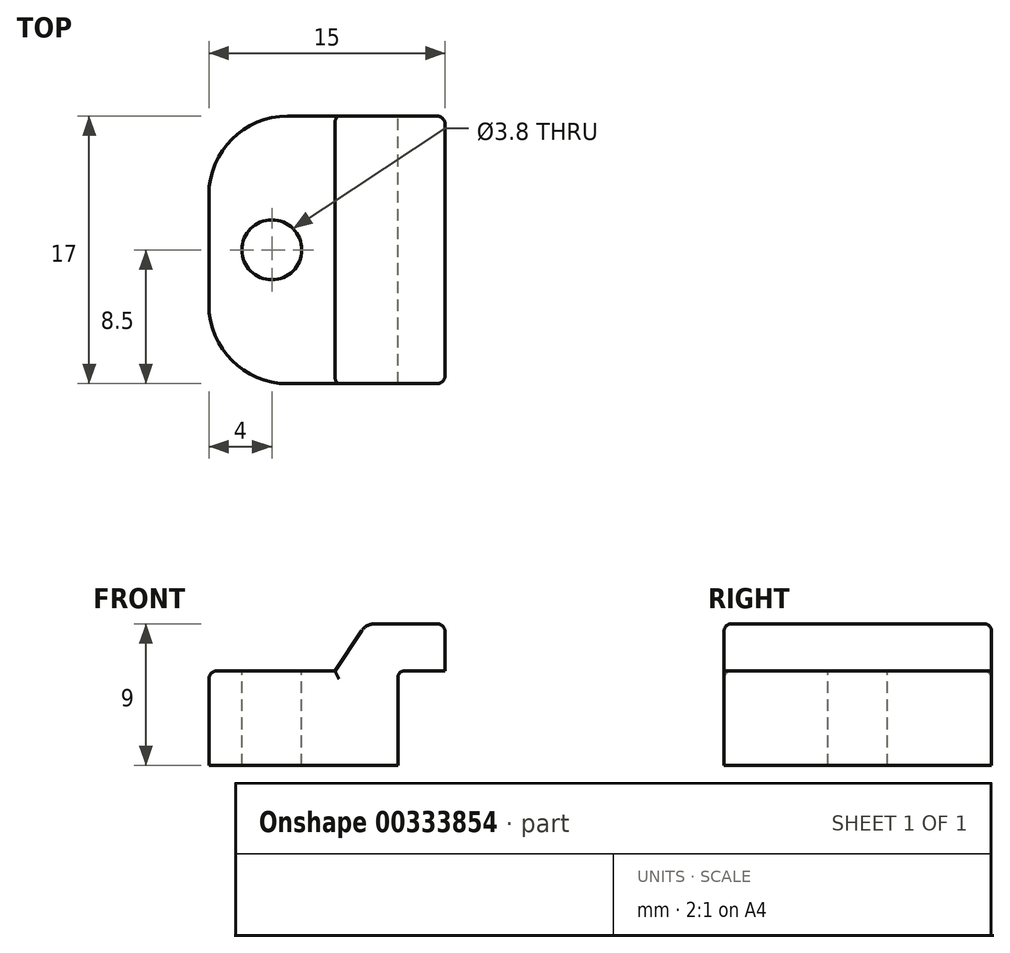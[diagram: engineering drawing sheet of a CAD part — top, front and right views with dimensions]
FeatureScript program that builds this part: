
annotation { "Feature Type Name" : "Feature", "Feature Type Description" : "" }
export const myFeature = defineFeature(function(context is Context, id is Id, definition is map)
    precondition{}
    {
        {
            var Q0;
            Q0=qCreatedBy(makeId("Front.planeOp"),FACE);
            var sketch = newSketch(context, id + "F0", { "sketchPlane" : qUnion([Q0])});
            skLineSegment(sketch, "E0", {"start": v(0, 0) * mm, "end": v(0, 5.59) * mm});
            skLineSegment(sketch, "E1", {"start": v(0.41, 6) * mm, "end": v(3, 6) * mm});
            skLineSegment(sketch, "E2", {"start": v(3, 6) * mm, "end": v(3, 9) * mm});
            skLineSegment(sketch, "E3", {"start": v(0, 0) * mm, "end": v(-12, 0) * mm});
            skLineSegment(sketch, "E4", {"start": v(-12, 0) * mm, "end": v(-12, 6) * mm});
            skLineSegment(sketch, "E5", {"start": v(-12, 6) * mm, "end": v(-2.83, 6) * mm});
            skLineSegment(sketch, "E6", {"start": v(3, 9) * mm, "end": v(-2, 9) * mm});
            skPoint(sketch, "E7.visualSharp", {"position": v(-4, 6) * mm});
            skPoint(sketch, "E8.visualSharp", {"position": v(1, 9) * mm});
            skPoint(sketch, "E9.visualSharp", {"position": v(0, 6) * mm});
            skArc(sketch, "E9.filletArc", {"start": v(0.41, 6) * mm, "mid": v(0.12, 5.88) * mm, "end": v(0, 5.59) * mm});
            skLineSegment(sketch, "E10", {"start": v(-4, 6) * mm, "end": v(-2.83, 6) * mm});
            skLineSegment(sketch, "E11", {"start": v(-2, 9) * mm, "end": v(-4, 6) * mm});
            skSolve(sketch);
        }
        {
            var Q0;
            Q0 = qSketchRegion(id + "F0", true);
            extrude(context, id + "F1", {"entities" : qUnion([Q0]), "depth" : 17 * mm});
        }
        {
            var Q0;
            Q0=makeQuery(id+"F1.opExtrude","SWEPT_EDGE",EDGE,{"disambiguationData":[OSD([sQuery(id+"F0.wireOp",EDGE,"E2"),sQuery(id+"F0.wireOp",EDGE,"E6")])]});
            fillet(context, id + "F2", {"entities" : qUnion([Q0]), "radius" : 0.5 * mm, "tangentPropagation" : true, "allowEdgeOverflow" : false});
        }
        {
            var Q0;
            Q0=makeQuery(id+"F1.opExtrude","SWEPT_FACE",FACE,{"disambiguationData":[OSD([sQuery(id+"F0.wireOp",EDGE,"E5")])]});
            var sketch = newSketch(context, id + "F3", { "sketchPlane" : qUnion([Q0])});
            skCircle(sketch, "E12", {"center": v(-8, -8.5) * mm, "radius": 1.9 * mm});
            skPoint(sketch, "E12.centerSnap0", {"position": v(-8, -17) * mm});
            skPoint(sketch, "E12.centerSnap1", {"position": v(-12, -8.5) * mm});
            skSolve(sketch);
        }
        {
            var Q0;
            Q0 = qSketchRegion(id + "F3", true);
            extrude(context, id + "F4", {"entities" : qUnion([Q0]), "operationType" : NewBodyOperationType.REMOVE, "oppositeDirection" : true, "depth" : 25 * mm});
        }
        {
            var Q0;
            Q0=makeQuery(id+"F1.opExtrude","CAP_EDGE",EDGE,{"disambiguationData":[OSD([sQuery(id+"F0.wireOp",EDGE,"E4")])],"isStart":false});
            var Q1;
            Q1=makeQuery(id+"F1.opExtrude","CAP_EDGE",EDGE,{"disambiguationData":[OSD([sQuery(id+"F0.wireOp",EDGE,"E4")])],"isStart":true});
            fillet(context, id + "F5", {"entities" : qUnion([Q0, Q1]), "radius" : 5 * mm, "tangentPropagation" : true, "allowEdgeOverflow" : false});
        }
        {
            var Q0;
            Q0=makeQuery(id+"F5.opFillet","BLEND_EDGE",EDGE,{"blendedFrom":[makeQuery(id+"F1.opExtrude","CAP_EDGE",EDGE,{"disambiguationData":[OSD([sQuery(id+"F0.wireOp",EDGE,"E4")])],"isStart":false}),makeQuery(id+"F1.opExtrude","SWEPT_FACE",FACE,{"disambiguationData":[OSD([sQuery(id+"F0.wireOp",EDGE,"E5")])]})],"blendedInto":[makeQuery(id+"F1.opExtrude","SWEPT_FACE",FACE,{"disambiguationData":[OSD([sQuery(id+"F0.wireOp",EDGE,"E5")])]})]});
            fillet(context, id + "F6", {"entities" : qUnion([Q0]), "radius" : 0.5 * mm, "tangentPropagation" : true, "allowEdgeOverflow" : false});
        }
        {
            var Q0;
            Q0=makeQuery(id+"F1.opExtrude","SWEPT_EDGE",EDGE,{"disambiguationData":[OSD([sQuery(id+"F0.wireOp",EDGE,"E6"),sQuery(id+"F0.wireOp",EDGE,"E11")])]});
            fillet(context, id + "F7", {"entities" : qUnion([Q0]), "radius" : 1 * mm, "tangentPropagation" : true, "allowEdgeOverflow" : false});
        }
        {
            var Q0;
            Q0=makeQuery(id+"F1.opExtrude","CAP_EDGE",EDGE,{"disambiguationData":[OSD([sQuery(id+"F0.wireOp",EDGE,"E11")])],"isStart":false});
            var Q1;
            Q1=makeQuery(id+"F1.opExtrude","CAP_EDGE",EDGE,{"disambiguationData":[OSD([sQuery(id+"F0.wireOp",EDGE,"E11")])],"isStart":true});
            fillet(context, id + "F8", {"entities" : qUnion([Q0, Q1]), "radius" : 0.5 * mm, "tangentPropagation" : true, "allowEdgeOverflow" : false});
        }
    });
